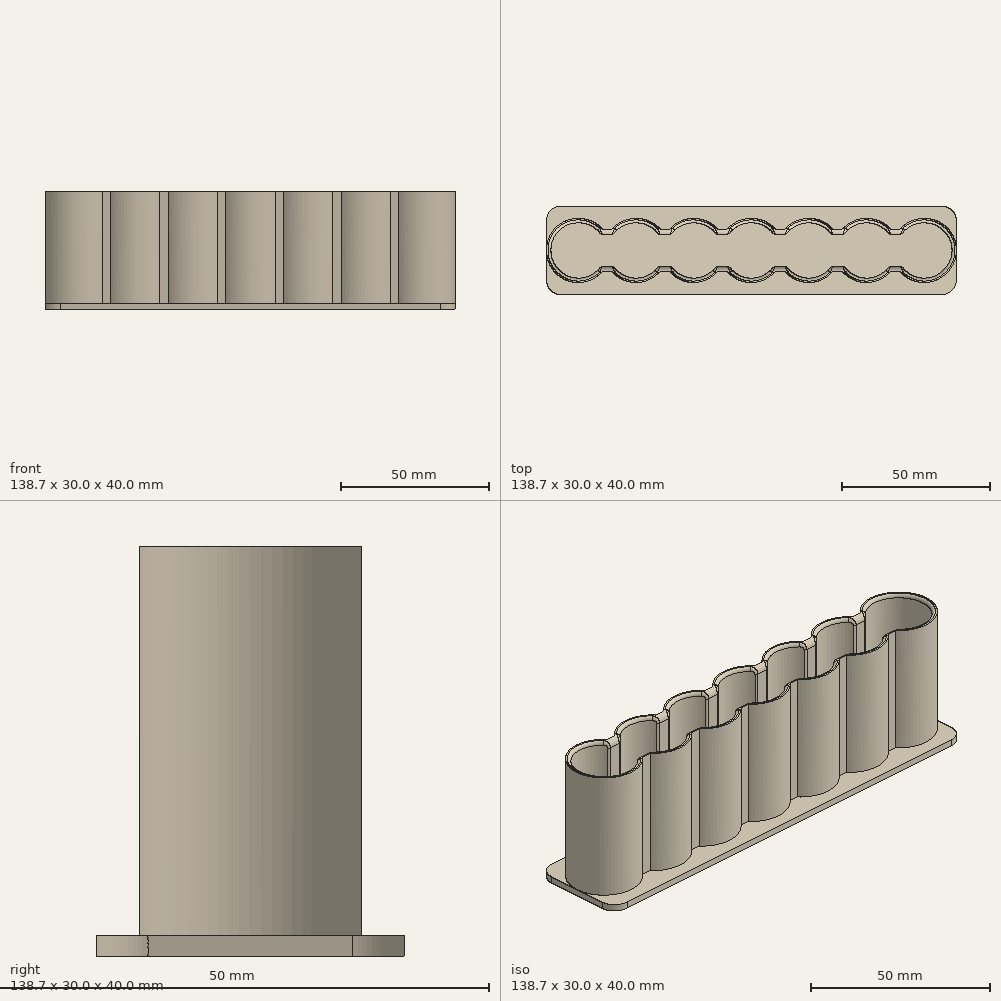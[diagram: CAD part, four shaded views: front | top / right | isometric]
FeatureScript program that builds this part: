
annotation { "Feature Type Name" : "Feature", "Feature Type Description" : "" }
export const myFeature = defineFeature(function(context is Context, id is Id, definition is map)
    precondition{}
    {
        {
            var Q0;
            Q0=qCreatedBy(makeId("Top.planeOp"),FACE);
            var sketch = newSketch(context, id + "F0", { "sketchPlane" : qUnion([Q0])});
            skArc(sketch, "E0", {"start": v(7.56, 5.5) * mm, "mid": v(-9.35, 0) * mm, "end": v(7.56, -5.5) * mm});
            skArc(sketch, "E1.1.0.0", {"start": v(11.94, -5.5) * mm, "mid": v(19.5, -9.35) * mm, "end": v(27.06, -5.5) * mm});
            skArc(sketch, "E1.2.0.0", {"start": v(31.44, -5.5) * mm, "mid": v(39, -9.35) * mm, "end": v(46.56, -5.5) * mm});
            skLineSegment(sketch, "E1.direction1", {"start": v(0, 0) * mm, "end": v(19.5, 0) * mm, "construction": true});
            skArc(sketch, "E2.0.3.0", {"start": v(50.94, -5.5) * mm, "mid": v(58.5, -9.35) * mm, "end": v(66.06, -5.5) * mm});
            skArc(sketch, "E2.0.4.0", {"start": v(70.44, -5.5) * mm, "mid": v(78, -9.35) * mm, "end": v(85.56, -5.5) * mm});
            skArc(sketch, "E2.0.5.0", {"start": v(89.94, -5.5) * mm, "mid": v(97.5, -9.35) * mm, "end": v(105.06, -5.5) * mm});
            skArc(sketch, "E2.0.6.0", {"start": v(109.44, -5.5) * mm, "mid": v(126.35, 0) * mm, "end": v(109.44, 5.5) * mm});
            skLineSegment(sketch, "E3", {"start": v(7.56, 5.5) * mm, "end": v(11.94, 5.5) * mm});
            skLineSegment(sketch, "E4.trimOffspring", {"start": v(27.06, 5.5) * mm, "end": v(31.44, 5.5) * mm});
            skLineSegment(sketch, "E5.trimOffspring", {"start": v(46.56, 5.5) * mm, "end": v(50.94, 5.5) * mm});
            skLineSegment(sketch, "E6.trimOffspring", {"start": v(66.06, 5.5) * mm, "end": v(70.44, 5.5) * mm});
            skLineSegment(sketch, "E7.trimOffspring", {"start": v(85.56, 5.5) * mm, "end": v(89.94, 5.5) * mm});
            skLineSegment(sketch, "E8.trimOffspring", {"start": v(105.06, 5.5) * mm, "end": v(109.44, 5.5) * mm});
            skLineSegment(sketch, "E9.MirrorCS", {"start": v(7.56, -5.5) * mm, "end": v(11.94, -5.5) * mm});
            skLineSegment(sketch, "E10.MirrorCS", {"start": v(27.06, -5.5) * mm, "end": v(31.44, -5.5) * mm});
            skLineSegment(sketch, "E11.MirrorCS", {"start": v(46.56, -5.5) * mm, "end": v(50.94, -5.5) * mm});
            skLineSegment(sketch, "E12.MirrorCS", {"start": v(66.06, -5.5) * mm, "end": v(70.44, -5.5) * mm});
            skLineSegment(sketch, "E13.MirrorCS", {"start": v(85.56, -5.5) * mm, "end": v(89.94, -5.5) * mm});
            skLineSegment(sketch, "E14.MirrorCS", {"start": v(105.06, -5.5) * mm, "end": v(109.44, -5.5) * mm});
            skArc(sketch, "E15.trimOffspring", {"start": v(27.06, 5.5) * mm, "mid": v(19.5, 9.35) * mm, "end": v(11.94, 5.5) * mm});
            skArc(sketch, "E16.trimOffspring", {"start": v(46.56, 5.5) * mm, "mid": v(39, 9.35) * mm, "end": v(31.44, 5.5) * mm});
            skArc(sketch, "E17.trimOffspring", {"start": v(66.06, 5.5) * mm, "mid": v(58.5, 9.35) * mm, "end": v(50.94, 5.5) * mm});
            skArc(sketch, "E18.trimOffspring", {"start": v(85.56, 5.5) * mm, "mid": v(78, 9.35) * mm, "end": v(70.44, 5.5) * mm});
            skArc(sketch, "E19.trimOffspring", {"start": v(105.06, 5.5) * mm, "mid": v(97.5, 9.35) * mm, "end": v(89.94, 5.5) * mm});
            skArc(sketch, "E20.0", {"start": v(105.79, 7) * mm, "mid": v(97.5, 10.85) * mm, "end": v(89.21, 7) * mm});
            skArc(sketch, "E20.1", {"start": v(8.29, 7) * mm, "mid": v(-10.85, 0) * mm, "end": v(8.29, -7) * mm});
            skArc(sketch, "E20.3", {"start": v(47.29, 7) * mm, "mid": v(39, 10.85) * mm, "end": v(30.71, 7) * mm});
            skArc(sketch, "E20.6", {"start": v(86.29, 7) * mm, "mid": v(78, 10.85) * mm, "end": v(69.71, 7) * mm});
            skArc(sketch, "E20.7", {"start": v(30.71, -7) * mm, "mid": v(39, -10.85) * mm, "end": v(47.29, -7) * mm});
            skArc(sketch, "E20.8", {"start": v(50.21, -7) * mm, "mid": v(58.5, -10.85) * mm, "end": v(66.79, -7) * mm});
            skArc(sketch, "E20.10", {"start": v(89.21, -7) * mm, "mid": v(97.5, -10.85) * mm, "end": v(105.79, -7) * mm});
            skLineSegment(sketch, "E21", {"start": v(8.29, 7) * mm, "end": v(11.21, 7) * mm});
            skLineSegment(sketch, "E22.MirrorCS", {"start": v(8.29, -7) * mm, "end": v(11.21, -7) * mm});
            skLineSegment(sketch, "E23.1.0.0", {"start": v(27.79, 7) * mm, "end": v(30.71, 7) * mm});
            skLineSegment(sketch, "E23.2.0.0", {"start": v(47.29, 7) * mm, "end": v(50.21, 7) * mm});
            skLineSegment(sketch, "E23.3.0.0", {"start": v(66.79, 7) * mm, "end": v(69.71, 7) * mm});
            skLineSegment(sketch, "E23.4.0.0", {"start": v(86.29, 7) * mm, "end": v(89.21, 7) * mm});
            skLineSegment(sketch, "E23.5.0.0", {"start": v(105.79, 7) * mm, "end": v(108.71, 7) * mm});
            skLineSegment(sketch, "E24.MirrorCS", {"start": v(27.79, -7) * mm, "end": v(30.71, -7) * mm});
            skLineSegment(sketch, "E25.MirrorCS", {"start": v(47.29, -7) * mm, "end": v(50.21, -7) * mm});
            skLineSegment(sketch, "E26.MirrorCS", {"start": v(66.79, -7) * mm, "end": v(69.71, -7) * mm});
            skLineSegment(sketch, "E27.MirrorCS", {"start": v(86.29, -7) * mm, "end": v(89.21, -7) * mm});
            skLineSegment(sketch, "E28.MirrorCS", {"start": v(105.79, -7) * mm, "end": v(108.71, -7) * mm});
            skArc(sketch, "E29.trimOffspring", {"start": v(27.79, 7) * mm, "mid": v(19.5, 10.85) * mm, "end": v(11.21, 7) * mm});
            skArc(sketch, "E30.trimOffspring", {"start": v(66.79, 7) * mm, "mid": v(58.5, 10.85) * mm, "end": v(50.21, 7) * mm});
            skArc(sketch, "E31.trimOffspring", {"start": v(11.21, -7) * mm, "mid": v(19.5, -10.85) * mm, "end": v(27.79, -7) * mm});
            skArc(sketch, "E32.trimOffspring", {"start": v(69.71, -7) * mm, "mid": v(78, -10.85) * mm, "end": v(86.29, -7) * mm});
            skArc(sketch, "E33.trimOffspring", {"start": v(108.71, -7) * mm, "mid": v(127.85, 0) * mm, "end": v(108.71, 7) * mm});
            skSolve(sketch);
        }
        {
            var Q0;
            Q0=qCreatedBy(makeId("Top.planeOp"),FACE);
            var sketch = newSketch(context, id + "F1", { "sketchPlane" : qUnion([Q0])});
            skArc(sketch, "E34", {"start": v(7.52, 5.55) * mm, "mid": v(-9.35, 0) * mm, "end": v(7.52, -5.55) * mm});
            skArc(sketch, "E35.2.0.0", {"start": v(29.28, -5.55) * mm, "mid": v(36.8, -9.35) * mm, "end": v(44.32, -5.55) * mm});
            skLineSegment(sketch, "E35.direction1", {"start": v(0, 0) * mm, "end": v(18.5, 0) * mm, "construction": true});
            skArc(sketch, "E36.0", {"start": v(8.15, 7.16) * mm, "mid": v(-10.85, 0) * mm, "end": v(8.15, -7.16) * mm});
            skArc(sketch, "E37.0", {"start": v(28.65, -7.16) * mm, "mid": v(36.8, -10.85) * mm, "end": v(44.95, -7.16) * mm});
            skLineSegment(sketch, "E38", {"start": v(8.15, 7.16) * mm, "end": v(10.25, 7.16) * mm});
            skLineSegment(sketch, "E39.1.0.0", {"start": v(26.55, 7.16) * mm, "end": v(28.65, 7.16) * mm});
            skLineSegment(sketch, "E39.direction1", {"start": v(8.15, 7.16) * mm, "end": v(10.25, 7.16) * mm, "construction": true});
            skLineSegment(sketch, "E40", {"start": v(9.2, 5.55) * mm, "end": v(7.52, 5.55) * mm});
            skLineSegment(sketch, "E41", {"start": v(7.52, 5.55) * mm, "end": v(10.88, 5.55) * mm});
            skLineSegment(sketch, "E42.MirrorCS", {"start": v(8.15, -7.16) * mm, "end": v(10.25, -7.16) * mm});
            skLineSegment(sketch, "E43.MirrorCS", {"start": v(7.52, -5.55) * mm, "end": v(10.88, -5.55) * mm});
            skLineSegment(sketch, "E44.MirrorCS", {"start": v(26.55, -7.16) * mm, "end": v(28.65, -7.16) * mm});
            skLineSegment(sketch, "E45.MirrorCS", {"start": v(25.68, -5.55) * mm, "end": v(29.28, -5.55) * mm});
            skArc(sketch, "E46.trimOffspring", {"start": v(10.25, -7.16) * mm, "mid": v(18.4, -10.93) * mm, "end": v(26.55, -7.16) * mm});
            skArc(sketch, "E47.trimOffspring", {"start": v(10.88, -5.55) * mm, "mid": v(18.28, -9.29) * mm, "end": v(25.68, -5.55) * mm});
            skArc(sketch, "E48.trimOffspring", {"start": v(26.55, 7.16) * mm, "mid": v(18.4, 10.93) * mm, "end": v(10.25, 7.16) * mm});
            skArc(sketch, "E49.trimOffspring", {"start": v(25.68, 5.55) * mm, "mid": v(18.28, 9.29) * mm, "end": v(10.88, 5.55) * mm});
            skLineSegment(sketch, "E50", {"start": v(25.68, 5.55) * mm, "end": v(29.28, 5.55) * mm});
            skArc(sketch, "E51", {"start": v(62.82, 5.55) * mm, "mid": v(55.3, 9.35) * mm, "end": v(47.78, 5.55) * mm});
            skArc(sketch, "E52.2.0.0", {"start": v(84.58, -5.55) * mm, "mid": v(101.45, 0) * mm, "end": v(84.58, 5.55) * mm});
            skLineSegment(sketch, "E52.direction1", {"start": v(55.3, 0) * mm, "end": v(73.8, 0) * mm, "construction": true});
            skArc(sketch, "E53.0", {"start": v(63.45, 7.16) * mm, "mid": v(55.3, 10.85) * mm, "end": v(47.15, 7.16) * mm});
            skArc(sketch, "E54.0", {"start": v(83.95, -7.16) * mm, "mid": v(102.95, 0) * mm, "end": v(83.95, 7.16) * mm});
            skLineSegment(sketch, "E55", {"start": v(63.45, 7.16) * mm, "end": v(65.55, 7.16) * mm});
            skLineSegment(sketch, "E56.1.0.0", {"start": v(81.85, 7.16) * mm, "end": v(83.95, 7.16) * mm});
            skLineSegment(sketch, "E56.direction1", {"start": v(63.45, 7.16) * mm, "end": v(65.55, 7.16) * mm, "construction": true});
            skLineSegment(sketch, "E57", {"start": v(64.5, 5.55) * mm, "end": v(62.82, 5.55) * mm});
            skLineSegment(sketch, "E58", {"start": v(62.82, 5.55) * mm, "end": v(66.18, 5.55) * mm});
            skLineSegment(sketch, "E59.MirrorCS", {"start": v(63.45, -7.16) * mm, "end": v(65.55, -7.16) * mm});
            skLineSegment(sketch, "E60.MirrorCS", {"start": v(62.82, -5.55) * mm, "end": v(66.18, -5.55) * mm});
            skLineSegment(sketch, "E61.MirrorCS", {"start": v(81.85, -7.16) * mm, "end": v(83.95, -7.16) * mm});
            skLineSegment(sketch, "E62.MirrorCS", {"start": v(80.98, -5.55) * mm, "end": v(84.58, -5.55) * mm});
            skArc(sketch, "E63.trimOffspring", {"start": v(65.55, -7.16) * mm, "mid": v(73.7, -10.93) * mm, "end": v(81.85, -7.16) * mm});
            skArc(sketch, "E64.trimOffspring", {"start": v(66.18, -5.55) * mm, "mid": v(73.58, -9.29) * mm, "end": v(80.98, -5.55) * mm});
            skArc(sketch, "E65.trimOffspring", {"start": v(81.85, 7.16) * mm, "mid": v(73.7, 10.93) * mm, "end": v(65.55, 7.16) * mm});
            skArc(sketch, "E66.trimOffspring", {"start": v(80.98, 5.55) * mm, "mid": v(73.58, 9.29) * mm, "end": v(66.18, 5.55) * mm});
            skLineSegment(sketch, "E67", {"start": v(80.98, 5.55) * mm, "end": v(84.58, 5.55) * mm});
            skLineSegment(sketch, "E68.0.3.0", {"start": v(63.35, 7.16) * mm, "end": v(65.45, 7.16) * mm});
            skLineSegment(sketch, "E69", {"start": v(44.95, 7.16) * mm, "end": v(47.15, 7.16) * mm});
            skLineSegment(sketch, "E70", {"start": v(44.95, -7.16) * mm, "end": v(47.15, -7.16) * mm});
            skLineSegment(sketch, "E71", {"start": v(44.32, -5.55) * mm, "end": v(47.78, -5.55) * mm});
            skLineSegment(sketch, "E72", {"start": v(44.32, 5.55) * mm, "end": v(47.78, 5.55) * mm});
            skPoint(sketch, "E72.startSnap0", {"position": v(27.48, 5.55) * mm});
            skArc(sketch, "E73.trimOffspring", {"start": v(44.95, 7.16) * mm, "mid": v(36.8, 10.85) * mm, "end": v(28.65, 7.16) * mm});
            skArc(sketch, "E74.trimOffspring", {"start": v(46.05, 5.67) * mm, "mid": v(46.01, 5.61) * mm, "end": v(45.98, 5.55) * mm});
            skArc(sketch, "E75.trimOffspring", {"start": v(46.12, 5.55) * mm, "mid": v(46.09, 5.61) * mm, "end": v(46.05, 5.67) * mm});
            skArc(sketch, "E76.trimOffspring", {"start": v(47.78, -5.55) * mm, "mid": v(55.3, -9.35) * mm, "end": v(62.82, -5.55) * mm});
            skArc(sketch, "E77.trimOffspring", {"start": v(44.32, 5.55) * mm, "mid": v(36.8, 9.35) * mm, "end": v(29.28, 5.55) * mm});
            skArc(sketch, "E78.trimOffspring", {"start": v(45.98, -5.55) * mm, "mid": v(46.01, -5.61) * mm, "end": v(46.05, -5.67) * mm});
            skArc(sketch, "E79.trimOffspring", {"start": v(46.05, -5.67) * mm, "mid": v(46.09, -5.61) * mm, "end": v(46.12, -5.55) * mm});
            skArc(sketch, "E80.trimOffspring", {"start": v(47.15, -7.16) * mm, "mid": v(55.3, -10.85) * mm, "end": v(63.45, -7.16) * mm});
            skSolve(sketch);
        }
        {
            var Q0;
            Q0=makeQuery(id+"F0.imprint","IMPRINT",FACE,{"disambiguationData":[TD([[makeQuery(id+"F0.imprint","IMPRINT",EDGE,{"derivedFrom":sQuery(id+"F0.wireOp",EDGE,"E0")}),-1.0]])]});
            extrude(context, id + "F2", {"entities" : qUnion([Q0]), "depth" : 40 * mm, "offsetDistance" : 25 * mm});
        }
        {
            var Q0;
            Q0=qCreatedBy(makeId("Top.planeOp"),FACE);
            var sketch = newSketch(context, id + "F3", { "sketchPlane" : qUnion([Q0])});
            skLineSegment(sketch, "E81.bottom", {"start": v(-10.85, -15) * mm, "end": v(127.85, -15) * mm});
            skLineSegment(sketch, "E81.top", {"start": v(-10.85, 15) * mm, "end": v(127.85, 15) * mm});
            skLineSegment(sketch, "E81.left", {"start": v(-10.85, -15) * mm, "end": v(-10.85, 15) * mm});
            skLineSegment(sketch, "E81.right", {"start": v(127.85, -15) * mm, "end": v(127.85, 15) * mm});
            skPoint(sketch, "E81.middle", {"position": v(58.5, 0) * mm});
            skSolve(sketch);
        }
        {
            var Q0;
            Q0=makeQuery(id+"F3.imprint","IMPRINT",FACE,{"disambiguationData":[TD([[makeQuery(id+"F3.imprint","IMPRINT",EDGE,{"derivedFrom":sQuery(id+"F3.wireOp",EDGE,"E81.bottom")}),1.0]])]});
            extrude(context, id + "F4", {"entities" : qUnion([Q0]), "operationType" : NewBodyOperationType.ADD, "depth" : 2 * mm, "offsetDistance" : 25 * mm});
        }
        {
            var Q0;
            Q0=makeQuery(id+"F4.opExtrude","SWEPT_EDGE",EDGE,{"disambiguationData":[OSD([sQuery(id+"F3.wireOp",EDGE,"E81.bottom"),sQuery(id+"F3.wireOp",EDGE,"E81.left")])]});
            var Q1;
            Q1=makeQuery(id+"F4.opExtrude","SWEPT_EDGE",EDGE,{"disambiguationData":[OSD([sQuery(id+"F3.wireOp",EDGE,"E81.bottom"),sQuery(id+"F3.wireOp",EDGE,"E81.right")])]});
            var Q2;
            Q2=makeQuery(id+"F4.opExtrude","SWEPT_EDGE",EDGE,{"disambiguationData":[OSD([sQuery(id+"F3.wireOp",EDGE,"E81.top"),sQuery(id+"F3.wireOp",EDGE,"E81.left")])]});
            var Q3;
            Q3=makeQuery(id+"F4.opExtrude","SWEPT_EDGE",EDGE,{"disambiguationData":[OSD([sQuery(id+"F3.wireOp",EDGE,"E81.top"),sQuery(id+"F3.wireOp",EDGE,"E81.right")])]});
            fillet(context, id + "F5", {"entities" : qUnion([Q0, Q1, Q2, Q3]), "radius" : 5 * mm, "tangentPropagation" : true, "allowEdgeOverflow" : false});
        }
        {
            var Q0;
            Q0=qCreatedBy(makeId("Right.planeOp"),FACE);
            var sketch = newSketch(context, id + "F6", { "sketchPlane" : qUnion([Q0])});
            skLineSegment(sketch, "E82.bottom", {"start": v(-5.5, 2) * mm, "end": v(5.5, 2) * mm});
            skLineSegment(sketch, "E82.top", {"start": v(-5.5, 52) * mm, "end": v(5.5, 52) * mm});
            skLineSegment(sketch, "E82.left", {"start": v(-5.5, 2) * mm, "end": v(-5.5, 52) * mm});
            skLineSegment(sketch, "E82.right", {"start": v(5.5, 2) * mm, "end": v(5.5, 52) * mm});
            skPoint(sketch, "E82.middle", {"position": v(0, 27) * mm});
            skSolve(sketch);
        }
        {
            var Q0;
            Q0=makeQuery(id+"F2.opExtrude","CAP_EDGE",EDGE,{"disambiguationData":[OSD([sQuery(id+"F1.wireOp",EDGE,"E41")])],"isStart":false});
            var Q1;
            Q1=makeQuery(id+"F2.opExtrude","CAP_EDGE",EDGE,{"disambiguationData":[OSD([sQuery(id+"F1.wireOp",EDGE,"E50")])],"isStart":false});
            var Q2;
            {var subQ0=sQuery(id+"F1.wireOp",EDGE,"E72");Q2=makeQuery(id+"F2.opExtrude","CAP_EDGE",EDGE,{"disambiguationData":[OSD([subQ0]),TDD([makeQuery(id+"F1.imprint","IMPRINT",EDGE,{"disambiguationData":[TD([[makeQuery(id+"F1.imprint","INTERSECT",VERTEX,{"derivedFrom":[subQ0,sQuery(id+"F1.wireOp",EDGE,"E77.trimOffspring")]}),-1.0]])],"derivedFrom":subQ0})])],"isStart":false});}
            var Q3;
            Q3=makeQuery(id+"F2.opExtrude","CAP_EDGE",EDGE,{"disambiguationData":[OSD([sQuery(id+"F1.wireOp",EDGE,"E58")])],"isStart":false});
            var Q4;
            Q4=makeQuery(id+"F2.opExtrude","CAP_EDGE",EDGE,{"disambiguationData":[OSD([sQuery(id+"F1.wireOp",EDGE,"E67")])],"isStart":false});
            var Q5;
            Q5=makeQuery(id+"F2.opExtrude","CAP_EDGE",EDGE,{"disambiguationData":[OSD([sQuery(id+"F1.wireOp",EDGE,"E43.MirrorCS")])],"isStart":false});
            var Q6;
            Q6=makeQuery(id+"F2.opExtrude","CAP_EDGE",EDGE,{"disambiguationData":[OSD([sQuery(id+"F1.wireOp",EDGE,"E45.MirrorCS")])],"isStart":false});
            var Q7;
            {var subQ0=sQuery(id+"F1.wireOp",EDGE,"E71");Q7=makeQuery(id+"F2.opExtrude","CAP_EDGE",EDGE,{"disambiguationData":[OSD([subQ0]),TDD([makeQuery(id+"F1.imprint","IMPRINT",EDGE,{"disambiguationData":[TD([[makeQuery(id+"F1.imprint","INTERSECT",VERTEX,{"derivedFrom":[sQuery(id+"F1.wireOp",EDGE,"E35.2.0.0"),subQ0]}),-1.0]])],"derivedFrom":subQ0})])],"isStart":false});}
            var Q8;
            Q8=makeQuery(id+"F2.opExtrude","CAP_EDGE",EDGE,{"disambiguationData":[OSD([sQuery(id+"F1.wireOp",EDGE,"E60.MirrorCS")])],"isStart":false});
            var Q9;
            Q9=makeQuery(id+"F2.opExtrude","CAP_EDGE",EDGE,{"disambiguationData":[OSD([sQuery(id+"F1.wireOp",EDGE,"E62.MirrorCS")])],"isStart":false});
            var Q10;
            Q10=makeQuery(id+"FvLSEFZZQq34Obx_1.boolean.opBoolean","INTERSECT",EDGE,{"derivedFrom":[makeQuery(id+"F2.opExtrude","CAP_FACE",FACE,{"disambiguationData":[OSD([sQuery(id+"F1.wireOp",EDGE,"E34"),sQuery(id+"F1.wireOp",EDGE,"E35.2.0.0"),sQuery(id+"F1.wireOp",EDGE,"E36.0"),sQuery(id+"F1.wireOp",EDGE,"E37.0"),sQuery(id+"F1.wireOp",EDGE,"E38"),sQuery(id+"F1.wireOp",EDGE,"E39.1.0.0"),sQuery(id+"F1.wireOp",EDGE,"E41"),sQuery(id+"F1.wireOp",EDGE,"E42.MirrorCS"),sQuery(id+"F1.wireOp",EDGE,"E43.MirrorCS"),sQuery(id+"F1.wireOp",EDGE,"E44.MirrorCS"),sQuery(id+"F1.wireOp",EDGE,"E45.MirrorCS"),sQuery(id+"F1.wireOp",EDGE,"E46.trimOffspring"),sQuery(id+"F1.wireOp",EDGE,"E47.trimOffspring"),sQuery(id+"F1.wireOp",EDGE,"E48.trimOffspring"),sQuery(id+"F1.wireOp",EDGE,"E49.trimOffspring"),sQuery(id+"F1.wireOp",EDGE,"E50"),sQuery(id+"F1.wireOp",EDGE,"E51"),sQuery(id+"F1.wireOp",EDGE,"E52.2.0.0"),sQuery(id+"F1.wireOp",EDGE,"E53.0"),sQuery(id+"F1.wireOp",EDGE,"E54.0"),sQuery(id+"F1.wireOp",EDGE,"E55"),sQuery(id+"F1.wireOp",EDGE,"E56.1.0.0"),sQuery(id+"F1.wireOp",EDGE,"E58"),sQuery(id+"F1.wireOp",EDGE,"E59.MirrorCS"),sQuery(id+"F1.wireOp",EDGE,"E60.MirrorCS"),sQuery(id+"F1.wireOp",EDGE,"E61.MirrorCS"),sQuery(id+"F1.wireOp",EDGE,"E62.MirrorCS"),sQuery(id+"F1.wireOp",EDGE,"E63.trimOffspring"),sQuery(id+"F1.wireOp",EDGE,"E64.trimOffspring"),sQuery(id+"F1.wireOp",EDGE,"E65.trimOffspring"),sQuery(id+"F1.wireOp",EDGE,"E66.trimOffspring"),sQuery(id+"F1.wireOp",EDGE,"E67"),sQuery(id+"F1.wireOp",EDGE,"E68.0.3.0"),sQuery(id+"F1.wireOp",EDGE,"E69"),sQuery(id+"F1.wireOp",EDGE,"E70"),sQuery(id+"F1.wireOp",EDGE,"E71"),sQuery(id+"F1.wireOp",EDGE,"E72"),sQuery(id+"F1.wireOp",EDGE,"E73.trimOffspring"),sQuery(id+"F1.wireOp",EDGE,"E74.trimOffspring"),sQuery(id+"F1.wireOp",EDGE,"E75.trimOffspring"),sQuery(id+"F1.wireOp",EDGE,"E76.trimOffspring"),sQuery(id+"F1.wireOp",EDGE,"E77.trimOffspring"),sQuery(id+"F1.wireOp",EDGE,"E78.trimOffspring"),sQuery(id+"F1.wireOp",EDGE,"E79.trimOffspring"),sQuery(id+"F1.wireOp",EDGE,"E80.trimOffspring")])],"isStart":false}),makeQuery(id+"FvLSEFZZQq34Obx_1.opExtrude","SWEPT_FACE",FACE,{"disambiguationData":[OSD([sQuery(id+"F6.wireOp",EDGE,"E82.left")])]})]});
            var Q11;
            Q11=makeQuery(id+"FvLSEFZZQq34Obx_1.boolean.opBoolean","INTERSECT",EDGE,{"derivedFrom":[makeQuery(id+"F2.opExtrude","CAP_FACE",FACE,{"disambiguationData":[OSD([sQuery(id+"F1.wireOp",EDGE,"E34"),sQuery(id+"F1.wireOp",EDGE,"E35.2.0.0"),sQuery(id+"F1.wireOp",EDGE,"E36.0"),sQuery(id+"F1.wireOp",EDGE,"E37.0"),sQuery(id+"F1.wireOp",EDGE,"E38"),sQuery(id+"F1.wireOp",EDGE,"E39.1.0.0"),sQuery(id+"F1.wireOp",EDGE,"E41"),sQuery(id+"F1.wireOp",EDGE,"E42.MirrorCS"),sQuery(id+"F1.wireOp",EDGE,"E43.MirrorCS"),sQuery(id+"F1.wireOp",EDGE,"E44.MirrorCS"),sQuery(id+"F1.wireOp",EDGE,"E45.MirrorCS"),sQuery(id+"F1.wireOp",EDGE,"E46.trimOffspring"),sQuery(id+"F1.wireOp",EDGE,"E47.trimOffspring"),sQuery(id+"F1.wireOp",EDGE,"E48.trimOffspring"),sQuery(id+"F1.wireOp",EDGE,"E49.trimOffspring"),sQuery(id+"F1.wireOp",EDGE,"E50"),sQuery(id+"F1.wireOp",EDGE,"E51"),sQuery(id+"F1.wireOp",EDGE,"E52.2.0.0"),sQuery(id+"F1.wireOp",EDGE,"E53.0"),sQuery(id+"F1.wireOp",EDGE,"E54.0"),sQuery(id+"F1.wireOp",EDGE,"E55"),sQuery(id+"F1.wireOp",EDGE,"E56.1.0.0"),sQuery(id+"F1.wireOp",EDGE,"E58"),sQuery(id+"F1.wireOp",EDGE,"E59.MirrorCS"),sQuery(id+"F1.wireOp",EDGE,"E60.MirrorCS"),sQuery(id+"F1.wireOp",EDGE,"E61.MirrorCS"),sQuery(id+"F1.wireOp",EDGE,"E62.MirrorCS"),sQuery(id+"F1.wireOp",EDGE,"E63.trimOffspring"),sQuery(id+"F1.wireOp",EDGE,"E64.trimOffspring"),sQuery(id+"F1.wireOp",EDGE,"E65.trimOffspring"),sQuery(id+"F1.wireOp",EDGE,"E66.trimOffspring"),sQuery(id+"F1.wireOp",EDGE,"E67"),sQuery(id+"F1.wireOp",EDGE,"E68.0.3.0"),sQuery(id+"F1.wireOp",EDGE,"E69"),sQuery(id+"F1.wireOp",EDGE,"E70"),sQuery(id+"F1.wireOp",EDGE,"E71"),sQuery(id+"F1.wireOp",EDGE,"E72"),sQuery(id+"F1.wireOp",EDGE,"E73.trimOffspring"),sQuery(id+"F1.wireOp",EDGE,"E74.trimOffspring"),sQuery(id+"F1.wireOp",EDGE,"E75.trimOffspring"),sQuery(id+"F1.wireOp",EDGE,"E76.trimOffspring"),sQuery(id+"F1.wireOp",EDGE,"E77.trimOffspring"),sQuery(id+"F1.wireOp",EDGE,"E78.trimOffspring"),sQuery(id+"F1.wireOp",EDGE,"E79.trimOffspring"),sQuery(id+"F1.wireOp",EDGE,"E80.trimOffspring")])],"isStart":false}),makeQuery(id+"FvLSEFZZQq34Obx_1.opExtrude","SWEPT_FACE",FACE,{"disambiguationData":[OSD([sQuery(id+"F6.wireOp",EDGE,"E82.right")])]})]});
            var Q12;
            Q12=makeQuery(id+"F2.opExtrude","CAP_EDGE",EDGE,{"disambiguationData":[OSD([sQuery(id+"F0.wireOp",EDGE,"E3")])],"isStart":false});
            var Q13;
            Q13=makeQuery(id+"F2.opExtrude","CAP_EDGE",EDGE,{"disambiguationData":[OSD([sQuery(id+"F0.wireOp",EDGE,"E4.trimOffspring")])],"isStart":false});
            var Q14;
            Q14=makeQuery(id+"F2.opExtrude","CAP_EDGE",EDGE,{"disambiguationData":[OSD([sQuery(id+"F0.wireOp",EDGE,"E5.trimOffspring")])],"isStart":false});
            var Q15;
            Q15=makeQuery(id+"F2.opExtrude","CAP_EDGE",EDGE,{"disambiguationData":[OSD([sQuery(id+"F0.wireOp",EDGE,"E6.trimOffspring")])],"isStart":false});
            var Q16;
            Q16=makeQuery(id+"F2.opExtrude","CAP_EDGE",EDGE,{"disambiguationData":[OSD([sQuery(id+"F0.wireOp",EDGE,"E7.trimOffspring")])],"isStart":false});
            var Q17;
            Q17=makeQuery(id+"F2.opExtrude","CAP_EDGE",EDGE,{"disambiguationData":[OSD([sQuery(id+"F0.wireOp",EDGE,"E8.trimOffspring")])],"isStart":false});
            var Q18;
            Q18=makeQuery(id+"F2.opExtrude","CAP_EDGE",EDGE,{"disambiguationData":[OSD([sQuery(id+"F0.wireOp",EDGE,"E14.MirrorCS")])],"isStart":false});
            var Q19;
            Q19=makeQuery(id+"F2.opExtrude","CAP_EDGE",EDGE,{"disambiguationData":[OSD([sQuery(id+"F0.wireOp",EDGE,"E13.MirrorCS")])],"isStart":false});
            var Q20;
            Q20=makeQuery(id+"F2.opExtrude","CAP_EDGE",EDGE,{"disambiguationData":[OSD([sQuery(id+"F0.wireOp",EDGE,"E12.MirrorCS")])],"isStart":false});
            var Q21;
            Q21=makeQuery(id+"F2.opExtrude","CAP_EDGE",EDGE,{"disambiguationData":[OSD([sQuery(id+"F0.wireOp",EDGE,"E11.MirrorCS")])],"isStart":false});
            var Q22;
            Q22=makeQuery(id+"F2.opExtrude","CAP_EDGE",EDGE,{"disambiguationData":[OSD([sQuery(id+"F0.wireOp",EDGE,"E10.MirrorCS")])],"isStart":false});
            var Q23;
            Q23=makeQuery(id+"F2.opExtrude","CAP_EDGE",EDGE,{"disambiguationData":[OSD([sQuery(id+"F0.wireOp",EDGE,"E9.MirrorCS")])],"isStart":false});
            fillet(context, id + "F7", {"entities" : qUnion([Q0, Q1, Q2, Q3, Q4, Q5, Q6, Q7, Q8, Q9, Q10, Q11, Q12, Q13, Q14, Q15, Q16, Q17, Q18, Q19, Q20, Q21, Q22, Q23]), "radius" : 2 * mm, "tangentPropagation" : true, "allowEdgeOverflow" : false});
        }
        {
            var Q0;
            Q0=makeQuery(id+"F2.opExtrude","CAP_EDGE",EDGE,{"disambiguationData":[OSD([sQuery(id+"F0.wireOp",EDGE,"E0")])],"isStart":false});
            var Q1;
            Q1=makeQuery(id+"F2.opExtrude","CAP_EDGE",EDGE,{"disambiguationData":[OSD([sQuery(id+"F0.wireOp",EDGE,"E15.trimOffspring")])],"isStart":false});
            var Q2;
            Q2=makeQuery(id+"F2.opExtrude","CAP_EDGE",EDGE,{"disambiguationData":[OSD([sQuery(id+"F0.wireOp",EDGE,"E16.trimOffspring")])],"isStart":false});
            var Q3;
            Q3=makeQuery(id+"F2.opExtrude","CAP_EDGE",EDGE,{"disambiguationData":[OSD([sQuery(id+"F0.wireOp",EDGE,"E17.trimOffspring")])],"isStart":false});
            var Q4;
            Q4=makeQuery(id+"F2.opExtrude","CAP_EDGE",EDGE,{"disambiguationData":[OSD([sQuery(id+"F0.wireOp",EDGE,"E18.trimOffspring")])],"isStart":false});
            var Q5;
            Q5=makeQuery(id+"F2.opExtrude","CAP_EDGE",EDGE,{"disambiguationData":[OSD([sQuery(id+"F0.wireOp",EDGE,"E19.trimOffspring")])],"isStart":false});
            var Q6;
            Q6=makeQuery(id+"F2.opExtrude","CAP_EDGE",EDGE,{"disambiguationData":[OSD([sQuery(id+"F0.wireOp",EDGE,"E2.0.6.0")])],"isStart":false});
            var Q7;
            Q7=makeQuery(id+"F2.opExtrude","CAP_EDGE",EDGE,{"disambiguationData":[OSD([sQuery(id+"F0.wireOp",EDGE,"E2.0.5.0")])],"isStart":false});
            var Q8;
            Q8=makeQuery(id+"F2.opExtrude","CAP_EDGE",EDGE,{"disambiguationData":[OSD([sQuery(id+"F0.wireOp",EDGE,"E2.0.4.0")])],"isStart":false});
            var Q9;
            Q9=makeQuery(id+"F2.opExtrude","CAP_EDGE",EDGE,{"disambiguationData":[OSD([sQuery(id+"F0.wireOp",EDGE,"E2.0.3.0")])],"isStart":false});
            var Q10;
            Q10=makeQuery(id+"F2.opExtrude","CAP_EDGE",EDGE,{"disambiguationData":[OSD([sQuery(id+"F0.wireOp",EDGE,"E1.2.0.0")])],"isStart":false});
            var Q11;
            Q11=makeQuery(id+"F2.opExtrude","CAP_EDGE",EDGE,{"disambiguationData":[OSD([sQuery(id+"F0.wireOp",EDGE,"E1.1.0.0")])],"isStart":false});
            fillet(context, id + "F8", {"entities" : qUnion([Q0, Q1, Q2, Q3, Q4, Q5, Q6, Q7, Q8, Q9, Q10, Q11]), "radius" : 1 * mm, "tangentPropagation" : true, "allowEdgeOverflow" : false});
        }
    });
